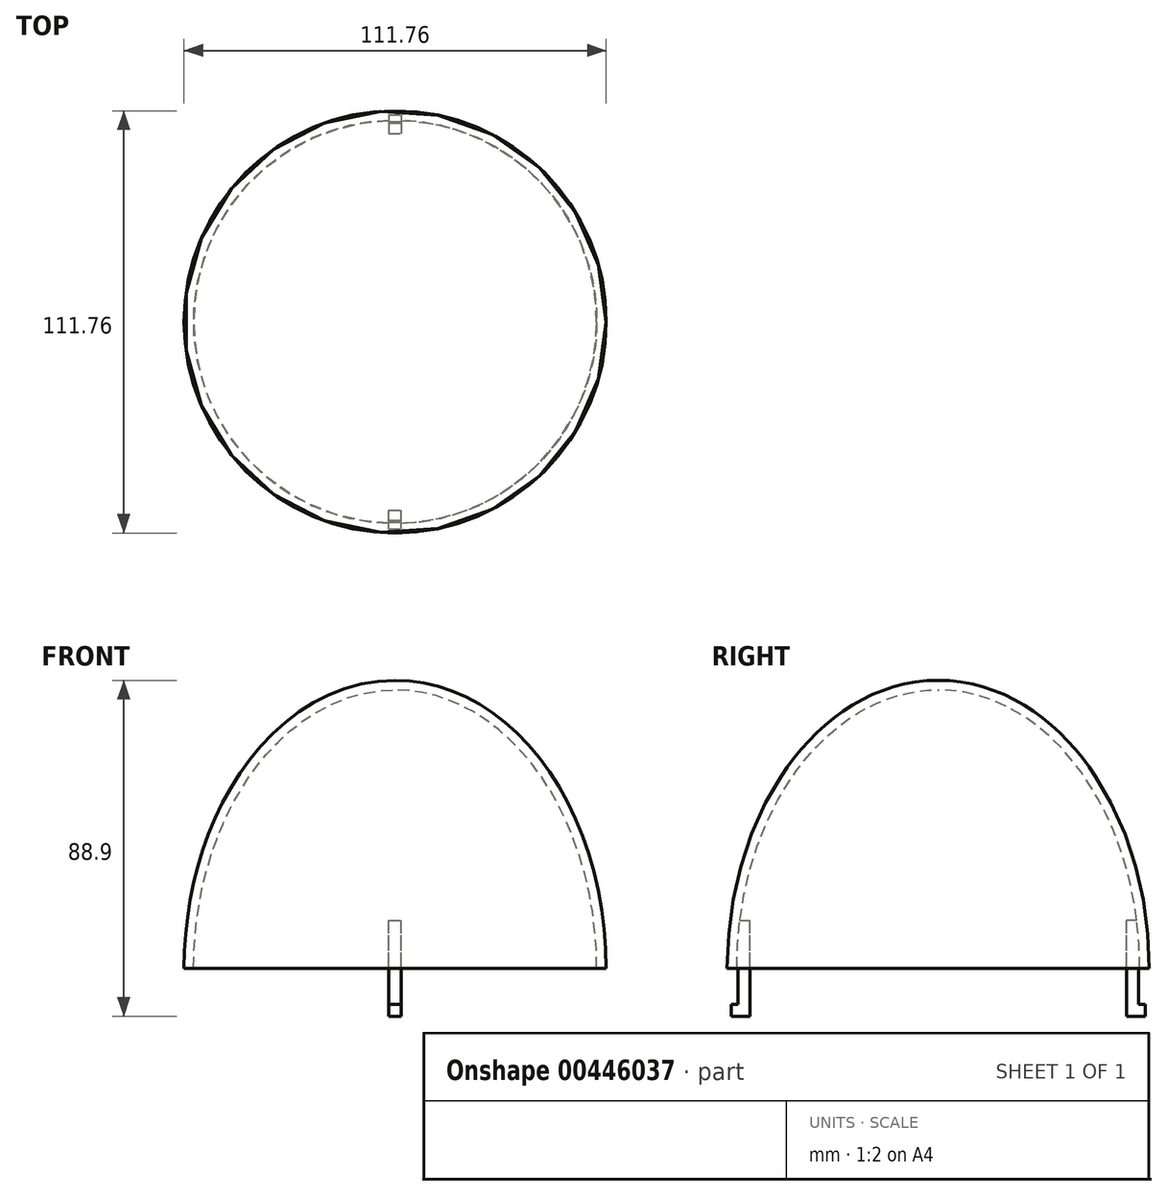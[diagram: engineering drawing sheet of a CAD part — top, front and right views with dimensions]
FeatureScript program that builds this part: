
annotation { "Feature Type Name" : "Feature", "Feature Type Description" : "" }
export const myFeature = defineFeature(function(context is Context, id is Id, definition is map)
    precondition{}
    {
        {
            var Q0;
            Q0=qCreatedBy(makeId("Front.planeOp"),FACE);
            var sketch = newSketch(context, id + "F0", { "sketchPlane" : qUnion([Q0])});
            skLineSegment(sketch, "E0", {"start": v(0, 105.43) * mm, "end": v(0, -46.97) * mm});
            skLineSegment(sketch, "E1", {"start": v(0, 29.23) * mm, "end": v(55.88, 29.23) * mm});
            skEllipse(sketch, "E2", {"center": v(0, 29.23) * mm, "majorRadius": 76.2 * mm, "minorRadius": 55.88 * mm, "majorAxis": v(0, 1)});
            skSolve(sketch);
        }
        {
            var Q0;
            {var subQ3=sQuery(id+"F0.wireOp",EDGE,"E1");Q0=makeQuery(id+"F0.imprint","IMPRINT",FACE,{"disambiguationData":[TD([[makeQuery(id+"F0.imprint","IMPRINT",EDGE,{"derivedFrom":subQ3}),1.0]])]});}
            var Q1;
            Q1=sQuery(id+"F0.wireOp",EDGE,"E0");
            revolve(context, id + "F1", {"entities" : qUnion([Q0]), "axis" : qUnion([Q1]), "revolveType" : RevolveType.FULL});
        }
        {
            var Q0;
            Q0=makeQuery(id+"F1.opRevolve","SWEPT_FACE",FACE,{"disambiguationData":[OSD([sQuery(id+"F0.wireOp",EDGE,"E1")])]});
            shell(context, id + "F2", {"entities" : qUnion([Q0]), "thickness" : 2.54 * mm});
        }
        {
            var Q0;
            Q0=makeQuery(id+"F1.opRevolve","SWEPT_FACE",FACE,{"disambiguationData":[OSD([sQuery(id+"F0.wireOp",EDGE,"E1")])]});
            var sketch = newSketch(context, id + "F3", { "sketchPlane" : qUnion([Q0])});
            skLineSegment(sketch, "E3.bottom", {"start": v(0, 54.75) * mm, "end": v(1.65, 54.75) * mm});
            skLineSegment(sketch, "E3.top", {"start": v(0, 49.82) * mm, "end": v(1.65, 49.82) * mm});
            skLineSegment(sketch, "E3.left", {"start": v(0, 54.75) * mm, "end": v(0, 49.82) * mm});
            skLineSegment(sketch, "E3.right", {"start": v(1.65, 54.75) * mm, "end": v(1.65, 49.82) * mm});
            skLineSegment(sketch, "E4.MirrorCS", {"start": v(0, 54.75) * mm, "end": v(-1.65, 54.75) * mm});
            skLineSegment(sketch, "E5.MirrorCS", {"start": v(-1.65, 54.75) * mm, "end": v(-1.65, 49.82) * mm});
            skLineSegment(sketch, "E6.MirrorCS", {"start": v(0, 49.82) * mm, "end": v(-1.65, 49.82) * mm});
            skSolve(sketch);
        }
        {
            var Q0;
            Q0 = qSketchRegion(id + "F3", true);
            extrude(context, id + "F4", {"entities" : qUnion([Q0]), "operationType" : NewBodyOperationType.ADD, "depth" : 12.7 * mm});
        }
        {
            var Q0;
            Q0=makeQuery(id+"F4.opExtrude","CAP_FACE",FACE,{"disambiguationData":[OSD([sQuery(id+"F3.wireOp",EDGE,"E3.bottom"),sQuery(id+"F3.wireOp",EDGE,"E3.top"),sQuery(id+"F3.wireOp",EDGE,"E3.right"),sQuery(id+"F3.wireOp",EDGE,"E4.MirrorCS"),sQuery(id+"F3.wireOp",EDGE,"E5.MirrorCS"),sQuery(id+"F3.wireOp",EDGE,"E6.MirrorCS")])],"isStart":false});
            extrude(context, id + "F5", {"entities" : qUnion([Q0]), "operationType" : NewBodyOperationType.ADD, "oppositeDirection" : true, "depth" : 25.4 * mm});
        }
        {
            var Q0;
            {var subQ0=sQuery(id+"F3.wireOp",EDGE,"E3.right");Q0=makeQuery(id+"F5.boolean.opBoolean","MERGE",FACE,{"derivedFrom":[makeQuery(id+"F4.opExtrude","SWEPT_FACE",FACE,{"disambiguationData":[OSD([subQ0])]}),makeQuery(id+"F5.opExtrude","SWEPT_FACE",FACE,{"disambiguationData":[OSD([subQ0])]})]});}
            var sketch = newSketch(context, id + "F6", { "sketchPlane" : qUnion([Q0])});
            skLineSegment(sketch, "E7.bottom", {"start": v(-54.75, 29.23) * mm, "end": v(-53.07, 29.23) * mm});
            skLineSegment(sketch, "E7.top", {"start": v(-54.75, 19.6) * mm, "end": v(-53.07, 19.6) * mm});
            skLineSegment(sketch, "E7.left", {"start": v(-54.75, 29.23) * mm, "end": v(-54.75, 19.6) * mm});
            skLineSegment(sketch, "E7.right", {"start": v(-53.07, 29.23) * mm, "end": v(-53.07, 19.6) * mm});
            skSolve(sketch);
        }
        {
            var Q0;
            Q0=makeQuery(id+"F6.imprint","IMPRINT",FACE,{"disambiguationData":[TD([[makeQuery(id+"F6.imprint","IMPRINT",EDGE,{"derivedFrom":sQuery(id+"F6.wireOp",EDGE,"E7.top")}),1.0]])]});
            extrude(context, id + "F7", {"entities" : qUnion([Q0]), "operationType" : NewBodyOperationType.REMOVE, "oppositeDirection" : true, "depth" : 25.4 * mm});
        }
        {
            var Q0;
            Q0=makeQuery(id+"F1.opRevolve","SWEPT_BODY",BODY,{"disambiguationData":[OSD([sQuery(id+"F0.wireOp",EDGE,"E0"),sQuery(id+"F0.wireOp",EDGE,"E1"),sQuery(id+"F0.wireOp",EDGE,"E2")])]});
            var Q1;
            Q1=qCreatedBy(makeId("Front.planeOp"),FACE);
            mirror(context, id + "F8", {"operationType" : NewBodyOperationType.ADD, "entities" : qUnion([Q0]), "mirrorPlane" : qUnion([Q1])});
        }
    });
